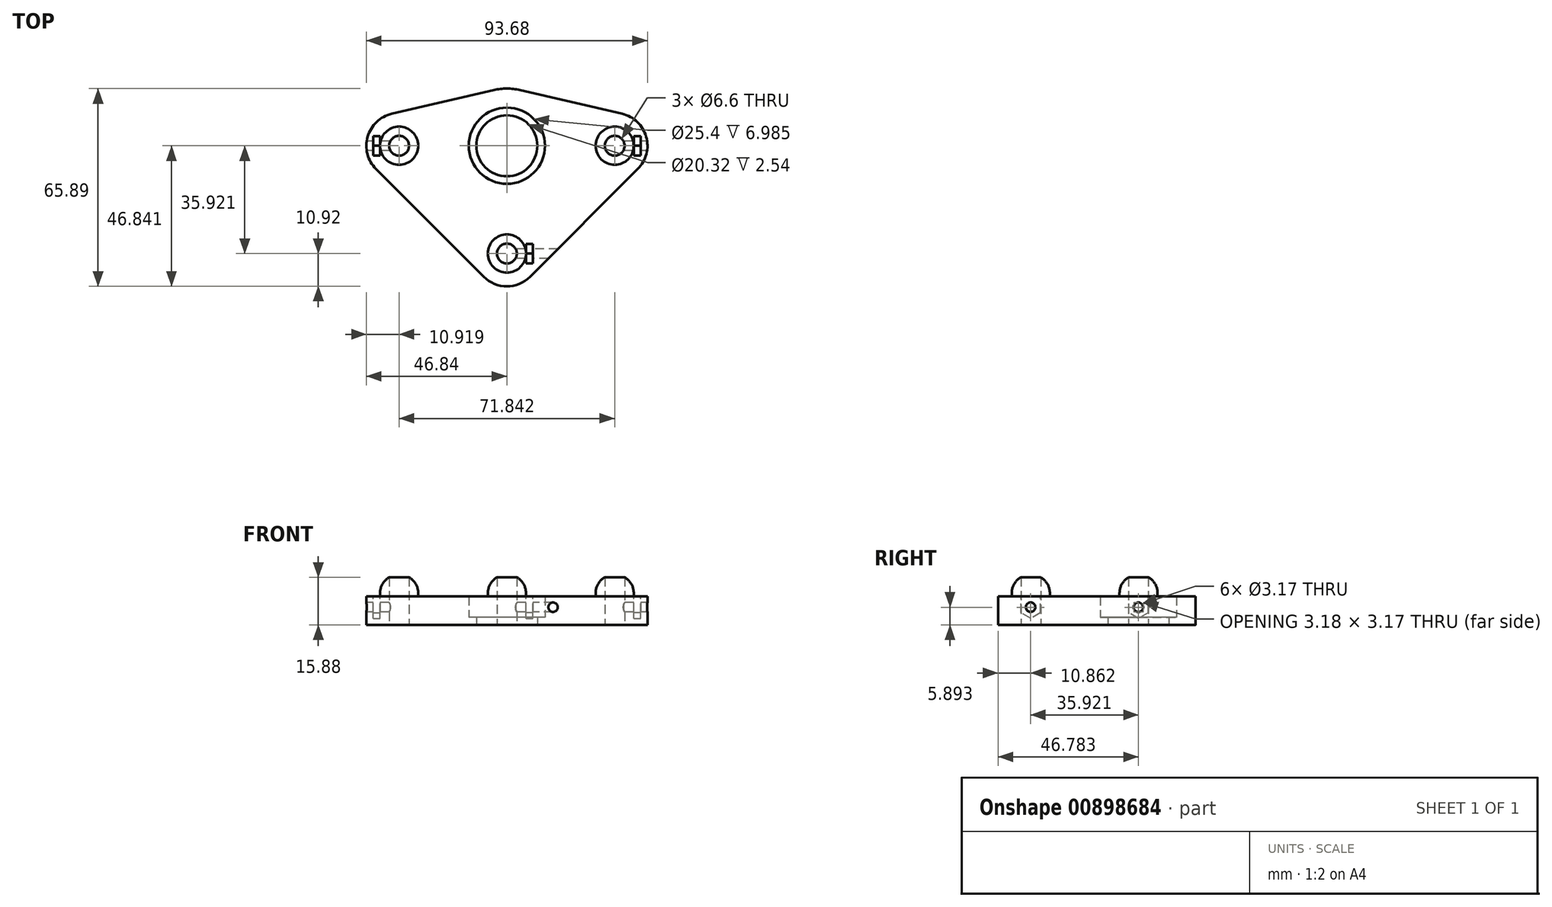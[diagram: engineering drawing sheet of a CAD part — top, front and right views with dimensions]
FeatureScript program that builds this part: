
annotation { "Feature Type Name" : "Feature", "Feature Type Description" : "" }
export const myFeature = defineFeature(function(context is Context, id is Id, definition is map)
    precondition{}
    {
        {
            var Q0;
            Q0=qCreatedBy(makeId("Top.planeOp"),FACE);
            var sketch = newSketch(context, id + "F0", { "sketchPlane" : qUnion([Q0])});
            skCircle(sketch, "E0", {"center": v(0, 35.92) * mm, "radius": 12.7 * mm});
            skArc(sketch, "E1.0", {"start": v(4.31, 54.48) * mm, "mid": v(0, 54.97) * mm, "end": v(-4.31, 54.48) * mm});
            skLineSegment(sketch, "E2", {"start": v(-38.4, 46.56) * mm, "end": v(-4.31, 54.48) * mm});
            skLineSegment(sketch, "E3", {"start": v(4.31, 54.48) * mm, "end": v(38.4, 46.56) * mm});
            skCircle(sketch, "E4.0", {"center": v(0, 35.92) * mm, "radius": 10.16 * mm});
            skLineSegment(sketch, "E5", {"start": v(0, 35.92) * mm, "end": v(0, 48.62) * mm, "construction": true});
            skLineSegment(sketch, "E6", {"start": v(-35.92, 35.92) * mm, "end": v(35.92, 35.92) * mm, "construction": true});
            skCircle(sketch, "E7", {"center": v(0, 0) * mm, "radius": 3.3 * mm});
            skCircle(sketch, "E8", {"center": v(35.92, 35.92) * mm, "radius": 3.3 * mm});
            skCircle(sketch, "E9", {"center": v(-35.92, 35.92) * mm, "radius": 3.3 * mm});
            skArc(sketch, "E10.0", {"start": v(-38.4, 46.56) * mm, "mid": v(-46.42, 38.92) * mm, "end": v(-43.64, 28.2) * mm});
            skArc(sketch, "E11.0", {"start": v(-7.72, -7.72) * mm, "mid": v(0, -10.92) * mm, "end": v(7.72, -7.72) * mm});
            skArc(sketch, "E12.0", {"start": v(43.64, 28.2) * mm, "mid": v(46.42, 38.92) * mm, "end": v(38.4, 46.56) * mm});
            skLineSegment(sketch, "E13", {"start": v(-43.64, 28.2) * mm, "end": v(-7.72, -7.72) * mm});
            skLineSegment(sketch, "E14", {"start": v(7.72, -7.72) * mm, "end": v(43.64, 28.2) * mm});
            skSolve(sketch);
        }
        {
            var Q0;
            Q0=makeQuery(id+"F0.imprint","IMPRINT",FACE,{"disambiguationData":[TD([[makeQuery(id+"F0.imprint","IMPRINT",EDGE,{"derivedFrom":sQuery(id+"F0.wireOp",EDGE,"E0")}),-1.0]])]});
            extrude(context, id + "F1", {"entities" : qUnion([Q0]), "depth" : 9.52 * mm, "offsetDistance" : 25.4 * mm});
        }
        {
            var Q0;
            Q0=makeQuery(id+"F0.imprint","IMPRINT",FACE,{"disambiguationData":[TD([[makeQuery(id+"F0.imprint","IMPRINT",EDGE,{"derivedFrom":sQuery(id+"F0.wireOp",EDGE,"E0")}),1.0]])]});
            var Q1;
            Q1=makeQuery(id+"F1.opExtrude","CAP_FACE",FACE,{"disambiguationData":[OSD([sQuery(id+"F0.wireOp",EDGE,"EjYE8rPL-0voM-13ep-dpKR-Yhmu4oC0fMjX"),sQuery(id+"F0.wireOp",EDGE,"BDsdlpYl-4XZS-kb72-SQzJ-jy24um5DGsSm"),sQuery(id+"F0.wireOp",EDGE,"zDj9rnkT-zBYQ-YRrf-FuGE-prHvdQQL9E0l"),sQuery(id+"F0.wireOp",EDGE,"E0"),sQuery(id+"F0.wireOp",EDGE,"be656b23-60e4-4951-9072-4bb9fd2c1fe0.0"),sQuery(id+"F0.wireOp",EDGE,"E1.0"),sQuery(id+"F0.wireOp",EDGE,"4a9f2f50-e787-4006-96f4-ab8e54a99077.0"),sQuery(id+"F0.wireOp",EDGE,"02fbeba7-076e-4ed0-9f02-67362b93dccf.0"),sQuery(id+"F0.wireOp",EDGE,"E2"),sQuery(id+"F0.wireOp",EDGE,"E3"),sQuery(id+"F0.wireOp",EDGE,"O9yRHGw0-B6N5-WUBC-CqYZ-9fVMz9zkHXct"),sQuery(id+"F0.wireOp",EDGE,"bXI39tXD-kIKO-QA8d-uo1d-AjNWw4kzWSzn"),sQuery(id+"F0.wireOp",EDGE,"yvXXFvSa-JQHm-aZvy-wO3q-0ffgoC5Wr51Q"),sQuery(id+"F0.wireOp",EDGE,"keBa6mA6-Ns36-as4S-D7yK-ubB9MYcM4YDE"),sQuery(id+"F0.wireOp",EDGE,"8eHimBAp-EooJ-JMgW-8GNK-FZK91k5yhUmU"),sQuery(id+"F0.wireOp",EDGE,"36RZBXD3-6qK0-qw5N-QxHJ-8RBiURi620yN"),sQuery(id+"F0.wireOp",EDGE,"1b80de2d-6fcf-4166-8bd7-bc7520118ab3.trimOffspring"),sQuery(id+"F0.wireOp",EDGE,"c2b8b45b-57a7-46a8-b7ff-993cbbd2993e.trimOffspring"),sQuery(id+"F0.wireOp",EDGE,"9e57da74-859c-4f91-937b-fdcaf8afdda5.filletArc"),sQuery(id+"F0.wireOp",EDGE,"30e6a12d-ff62-4460-809b-2951cf116d4f.filletArc"),sQuery(id+"F0.wireOp",EDGE,"3d167f00-72a4-4ff5-8a6d-0d591a0e7773.filletArc"),sQuery(id+"F0.wireOp",EDGE,"oY1VHBi5-08zZ-AYfj-pQcV-54PoHM0Vimur"),sQuery(id+"F0.wireOp",EDGE,"o9Ub0ZbI-FWSb-Ar0A-mzkB-0TMMgAmCBTNA"),sQuery(id+"F0.wireOp",EDGE,"02ed80ea-b338-46f1-988c-5186e078d909.trimOffspring"),sQuery(id+"F0.wireOp",EDGE,"5048e359-dd0b-4d89-8e95-103b38747b91.filletArc"),sQuery(id+"F0.wireOp",EDGE,"F9NU9Cbi-ggXa-7yM7-VtZo-IDbmedrVVywU"),sQuery(id+"F0.wireOp",EDGE,"RxFEJMYw-qQQS-0Qhc-ig3X-IfwXJgG6lVj4"),sQuery(id+"F0.wireOp",EDGE,"25558c64-657d-4b99-b26e-c29775e7ec7f.filletArc"),sQuery(id+"F0.wireOp",EDGE,"0ec6c237-3fc5-43e5-bd65-df81ba4ec1d8.filletArc"),sQuery(id+"F0.wireOp",EDGE,"df5fecd0-7309-4179-a44a-8c306f083116.filletArc"),sQuery(id+"F0.wireOp",EDGE,"e0a676b0-1f90-490a-bc8b-b1ab685ed8d2.filletArc")])],"isStart":false});
            extrude(context, id + "F2", {"entities" : qUnion([Q0]), "operationType" : NewBodyOperationType.ADD, "depth" : 2.54 * mm, "endBoundEntityFace" : qUnion([Q1]), "offsetDistance" : 6.35 * mm});
        }
        {
            var Q0;
            Q0=makeQuery(id+"F1.opExtrude","CAP_FACE",FACE,{"disambiguationData":[OSD([sQuery(id+"F0.wireOp",EDGE,"EjYE8rPL-0voM-13ep-dpKR-Yhmu4oC0fMjX"),sQuery(id+"F0.wireOp",EDGE,"BDsdlpYl-4XZS-kb72-SQzJ-jy24um5DGsSm"),sQuery(id+"F0.wireOp",EDGE,"zDj9rnkT-zBYQ-YRrf-FuGE-prHvdQQL9E0l"),sQuery(id+"F0.wireOp",EDGE,"E0"),sQuery(id+"F0.wireOp",EDGE,"be656b23-60e4-4951-9072-4bb9fd2c1fe0.0"),sQuery(id+"F0.wireOp",EDGE,"E1.0"),sQuery(id+"F0.wireOp",EDGE,"4a9f2f50-e787-4006-96f4-ab8e54a99077.0"),sQuery(id+"F0.wireOp",EDGE,"02fbeba7-076e-4ed0-9f02-67362b93dccf.0"),sQuery(id+"F0.wireOp",EDGE,"E2"),sQuery(id+"F0.wireOp",EDGE,"E3"),sQuery(id+"F0.wireOp",EDGE,"O9yRHGw0-B6N5-WUBC-CqYZ-9fVMz9zkHXct"),sQuery(id+"F0.wireOp",EDGE,"bXI39tXD-kIKO-QA8d-uo1d-AjNWw4kzWSzn"),sQuery(id+"F0.wireOp",EDGE,"yvXXFvSa-JQHm-aZvy-wO3q-0ffgoC5Wr51Q"),sQuery(id+"F0.wireOp",EDGE,"keBa6mA6-Ns36-as4S-D7yK-ubB9MYcM4YDE"),sQuery(id+"F0.wireOp",EDGE,"8eHimBAp-EooJ-JMgW-8GNK-FZK91k5yhUmU"),sQuery(id+"F0.wireOp",EDGE,"36RZBXD3-6qK0-qw5N-QxHJ-8RBiURi620yN"),sQuery(id+"F0.wireOp",EDGE,"1b80de2d-6fcf-4166-8bd7-bc7520118ab3.trimOffspring"),sQuery(id+"F0.wireOp",EDGE,"c2b8b45b-57a7-46a8-b7ff-993cbbd2993e.trimOffspring"),sQuery(id+"F0.wireOp",EDGE,"9e57da74-859c-4f91-937b-fdcaf8afdda5.filletArc"),sQuery(id+"F0.wireOp",EDGE,"30e6a12d-ff62-4460-809b-2951cf116d4f.filletArc"),sQuery(id+"F0.wireOp",EDGE,"3d167f00-72a4-4ff5-8a6d-0d591a0e7773.filletArc"),sQuery(id+"F0.wireOp",EDGE,"oY1VHBi5-08zZ-AYfj-pQcV-54PoHM0Vimur"),sQuery(id+"F0.wireOp",EDGE,"o9Ub0ZbI-FWSb-Ar0A-mzkB-0TMMgAmCBTNA"),sQuery(id+"F0.wireOp",EDGE,"02ed80ea-b338-46f1-988c-5186e078d909.trimOffspring"),sQuery(id+"F0.wireOp",EDGE,"3LgmcLzA-5pnU-fFz7-q1u9-bpeBtAsCO3An"),sQuery(id+"F0.wireOp",EDGE,"4eo9xTR6-c1Fu-en91-zOid-S4E7wj55DmDX"),sQuery(id+"F0.wireOp",EDGE,"5048e359-dd0b-4d89-8e95-103b38747b91.filletArc"),sQuery(id+"F0.wireOp",EDGE,"0de4be46-af92-408f-a28e-b5eb566cc358.filletArc"),sQuery(id+"F0.wireOp",EDGE,"cd97e584-8722-4711-bad1-4d169eb79cda.filletArc"),sQuery(id+"F0.wireOp",EDGE,"a80f9f6f-3806-41d0-9fd0-596e0330244b.filletArc"),sQuery(id+"F0.wireOp",EDGE,"743a1c7c-530f-41f0-bede-06812bb20fe3.filletArc")])],"isStart":false});
            var sketch = newSketch(context, id + "F3", { "sketchPlane" : qUnion([Q0])});
            skCircle(sketch, "E15", {"center": v(-35.92, 35.92) * mm, "radius": 6.35 * mm});
            skCircle(sketch, "E16", {"center": v(35.92, 35.92) * mm, "radius": 6.35 * mm});
            skCircle(sketch, "E17", {"center": v(0, 0) * mm, "radius": 6.35 * mm});
            skSolve(sketch);
        }
        {
            var Q0;
            Q0=makeQuery(id+"F1.opExtrude","CAP_FACE",FACE,{"disambiguationData":[OSD([sQuery(id+"F0.wireOp",EDGE,"EjYE8rPL-0voM-13ep-dpKR-Yhmu4oC0fMjX"),sQuery(id+"F0.wireOp",EDGE,"BDsdlpYl-4XZS-kb72-SQzJ-jy24um5DGsSm"),sQuery(id+"F0.wireOp",EDGE,"zDj9rnkT-zBYQ-YRrf-FuGE-prHvdQQL9E0l"),sQuery(id+"F0.wireOp",EDGE,"E0"),sQuery(id+"F0.wireOp",EDGE,"be656b23-60e4-4951-9072-4bb9fd2c1fe0.0"),sQuery(id+"F0.wireOp",EDGE,"E1.0"),sQuery(id+"F0.wireOp",EDGE,"4a9f2f50-e787-4006-96f4-ab8e54a99077.0"),sQuery(id+"F0.wireOp",EDGE,"02fbeba7-076e-4ed0-9f02-67362b93dccf.0"),sQuery(id+"F0.wireOp",EDGE,"E2"),sQuery(id+"F0.wireOp",EDGE,"E3"),sQuery(id+"F0.wireOp",EDGE,"O9yRHGw0-B6N5-WUBC-CqYZ-9fVMz9zkHXct"),sQuery(id+"F0.wireOp",EDGE,"bXI39tXD-kIKO-QA8d-uo1d-AjNWw4kzWSzn"),sQuery(id+"F0.wireOp",EDGE,"yvXXFvSa-JQHm-aZvy-wO3q-0ffgoC5Wr51Q"),sQuery(id+"F0.wireOp",EDGE,"keBa6mA6-Ns36-as4S-D7yK-ubB9MYcM4YDE"),sQuery(id+"F0.wireOp",EDGE,"8eHimBAp-EooJ-JMgW-8GNK-FZK91k5yhUmU"),sQuery(id+"F0.wireOp",EDGE,"36RZBXD3-6qK0-qw5N-QxHJ-8RBiURi620yN"),sQuery(id+"F0.wireOp",EDGE,"1b80de2d-6fcf-4166-8bd7-bc7520118ab3.trimOffspring"),sQuery(id+"F0.wireOp",EDGE,"c2b8b45b-57a7-46a8-b7ff-993cbbd2993e.trimOffspring"),sQuery(id+"F0.wireOp",EDGE,"9e57da74-859c-4f91-937b-fdcaf8afdda5.filletArc"),sQuery(id+"F0.wireOp",EDGE,"2f08ad09-a47d-42bd-8f0e-b7f58f6490e4.filletArc"),sQuery(id+"F0.wireOp",EDGE,"30e6a12d-ff62-4460-809b-2951cf116d4f.filletArc"),sQuery(id+"F0.wireOp",EDGE,"3d167f00-72a4-4ff5-8a6d-0d591a0e7773.filletArc"),sQuery(id+"F0.wireOp",EDGE,"oY1VHBi5-08zZ-AYfj-pQcV-54PoHM0Vimur"),sQuery(id+"F0.wireOp",EDGE,"o9Ub0ZbI-FWSb-Ar0A-mzkB-0TMMgAmCBTNA"),sQuery(id+"F0.wireOp",EDGE,"02ed80ea-b338-46f1-988c-5186e078d909.trimOffspring"),sQuery(id+"F0.wireOp",EDGE,"bfc3d6b4-ed7b-404a-8939-94d15189dd00.filletArc"),sQuery(id+"F0.wireOp",EDGE,"d06de643-c4a7-4e1d-b592-4d839de3a7a0.filletArc")])],"isStart":false});
            var sketch = newSketch(context, id + "F4", { "sketchPlane" : qUnion([Q0])});
            skPoint(sketch, "E18.center", {"position": v(0, 35.92) * mm});
            skCircle(sketch, "E19", {"center": v(-35.92, 35.92) * mm, "radius": 6.35 * mm});
            skCircle(sketch, "E20", {"center": v(35.92, 35.92) * mm, "radius": 6.35 * mm});
            skCircle(sketch, "E21", {"center": v(0, 0) * mm, "radius": 6.35 * mm});
            skLineSegment(sketch, "E22", {"start": v(-42.27, 39.15) * mm, "end": v(-42.27, 32.7) * mm});
            skLineSegment(sketch, "E23", {"start": v(-42.27, 32.7) * mm, "end": v(-44.6, 32.7) * mm});
            skLineSegment(sketch, "E24", {"start": v(-44.6, 32.7) * mm, "end": v(-44.6, 39.15) * mm});
            skLineSegment(sketch, "E25", {"start": v(-44.6, 39.15) * mm, "end": v(-42.27, 39.15) * mm});
            skLineSegment(sketch, "E26", {"start": v(-35.92, 35.92) * mm, "end": v(-42.27, 35.92) * mm, "construction": true});
            skLineSegment(sketch, "E27", {"start": v(42.27, 32.7) * mm, "end": v(42.27, 39.15) * mm});
            skLineSegment(sketch, "E28", {"start": v(42.27, 39.15) * mm, "end": v(44.6, 39.15) * mm});
            skLineSegment(sketch, "E29", {"start": v(44.6, 39.15) * mm, "end": v(44.6, 32.7) * mm});
            skLineSegment(sketch, "E30", {"start": v(44.6, 32.7) * mm, "end": v(42.27, 32.7) * mm});
            skLineSegment(sketch, "E31", {"start": v(35.92, 35.92) * mm, "end": v(42.27, 35.92) * mm, "construction": true});
            skLineSegment(sketch, "E32", {"start": v(8.69, 3.23) * mm, "end": v(8.69, -3.23) * mm});
            skLineSegment(sketch, "E33", {"start": v(8.69, -3.23) * mm, "end": v(6.35, -3.23) * mm});
            skLineSegment(sketch, "E34", {"start": v(6.35, -3.23) * mm, "end": v(6.35, 3.23) * mm});
            skLineSegment(sketch, "E35", {"start": v(6.35, 3.23) * mm, "end": v(8.69, 3.23) * mm});
            skLineSegment(sketch, "E36", {"start": v(8.69, 0) * mm, "end": v(0, 0) * mm, "construction": true});
            skSolve(sketch);
        }
        {
            var Q0;
            Q0=makeQuery(id+"F4.imprint","IMPRINT",FACE,{"disambiguationData":[TD([[makeQuery(id+"F4.imprint","IMPRINT",EDGE,{"derivedFrom":sQuery(id+"F4.wireOp",EDGE,"E18.2.0")}),-1.0]])]});
            var Q1;
            {var subQ3=sQuery(id+"F4.wireOp",EDGE,"d1FFw4VD-CotE-ErUC-aBlM-ySrozfUtPZIG");Q1=makeQuery(id+"F4.imprint","IMPRINT",FACE,{"disambiguationData":[TD([[makeQuery(id+"F4.imprint","IMPRINT",EDGE,{"derivedFrom":subQ3}),-1.0]])]});}
            var Q2;
            Q2=makeQuery(id+"F4.imprint","IMPRINT",FACE,{"disambiguationData":[TD([[makeQuery(id+"F4.imprint","IMPRINT",EDGE,{"derivedFrom":sQuery(id+"F4.wireOp",EDGE,"E18.1.0")}),-1.0]])]});
            var Q3;
            {var subQ0=sQuery(id+"F4.wireOp",EDGE,"E23");Q3=makeQuery(id+"F4.imprint","IMPRINT",FACE,{"disambiguationData":[TD([[makeQuery(id+"F4.imprint","IMPRINT",EDGE,{"derivedFrom":subQ0}),-1.0]])]});}
            var Q4;
            {var subQ0=sQuery(id+"F4.wireOp",EDGE,"E28");Q4=makeQuery(id+"F4.imprint","IMPRINT",FACE,{"disambiguationData":[TD([[makeQuery(id+"F4.imprint","IMPRINT",EDGE,{"derivedFrom":subQ0}),-1.0]])]});}
            var Q5;
            Q5=makeQuery(id+"F4.imprint","IMPRINT",FACE,{"disambiguationData":[TD([[makeQuery(id+"F4.imprint","IMPRINT",EDGE,{"derivedFrom":sQuery(id+"F4.wireOp",EDGE,"E32")}),-1.0]])]});
            extrude(context, id + "F5", {"entities" : qUnion([Q0, Q1, Q2, Q3, Q4, Q5]), "operationType" : NewBodyOperationType.REMOVE, "oppositeDirection" : true, "depth" : 8.64 * mm, "offsetDistance" : 25.4 * mm});
        }
        {
            var Q0;
            Q0=makeQuery(id+"F5.boolean.opBoolean","COPY",EDGE,{"derivedFrom":makeQuery(id+"F5.opExtrude","CAP_EDGE",EDGE,{"disambiguationData":[OSD([sQuery(id+"F4.wireOp",EDGE,"E18.1.1")])],"isStart":false})});
            var Q1;
            Q1=makeQuery(id+"F5.boolean.opBoolean","COPY",EDGE,{"derivedFrom":makeQuery(id+"F5.opExtrude","CAP_EDGE",EDGE,{"disambiguationData":[OSD([sQuery(id+"F4.wireOp",EDGE,"E18.1.3")])],"isStart":false})});
            var Q2;
            Q2=makeQuery(id+"F5.boolean.opBoolean","COPY",EDGE,{"derivedFrom":makeQuery(id+"F5.opExtrude","CAP_EDGE",EDGE,{"disambiguationData":[OSD([sQuery(id+"F4.wireOp",EDGE,"d1FFw4VD-CotE-ErUC-aBlM-ySrozfUtPZIG")])],"isStart":false})});
            var Q3;
            Q3=makeQuery(id+"F5.boolean.opBoolean","COPY",EDGE,{"derivedFrom":makeQuery(id+"F5.opExtrude","CAP_EDGE",EDGE,{"disambiguationData":[OSD([sQuery(id+"F4.wireOp",EDGE,"UtWCcdUI-wfrM-d3JI-pGr6-eE53RfRw4Zsa")])],"isStart":false})});
            var Q4;
            Q4=makeQuery(id+"F5.boolean.opBoolean","COPY",EDGE,{"derivedFrom":makeQuery(id+"F5.opExtrude","CAP_EDGE",EDGE,{"disambiguationData":[OSD([sQuery(id+"F4.wireOp",EDGE,"E18.2.3")])],"isStart":false})});
            var Q5;
            Q5=makeQuery(id+"F5.boolean.opBoolean","COPY",EDGE,{"derivedFrom":makeQuery(id+"F5.opExtrude","CAP_EDGE",EDGE,{"disambiguationData":[OSD([sQuery(id+"F4.wireOp",EDGE,"E18.2.1")])],"isStart":false})});
            var Q6;
            Q6=makeQuery(id+"F5.boolean.opBoolean","COPY",EDGE,{"derivedFrom":makeQuery(id+"F5.opExtrude","CAP_EDGE",EDGE,{"disambiguationData":[OSD([sQuery(id+"F4.wireOp",EDGE,"E25")])],"isStart":false})});
            var Q7;
            Q7=makeQuery(id+"F5.boolean.opBoolean","COPY",EDGE,{"derivedFrom":makeQuery(id+"F5.opExtrude","CAP_EDGE",EDGE,{"disambiguationData":[OSD([sQuery(id+"F4.wireOp",EDGE,"E23")])],"isStart":false})});
            var Q8;
            Q8=makeQuery(id+"F5.boolean.opBoolean","COPY",EDGE,{"derivedFrom":makeQuery(id+"F5.opExtrude","CAP_EDGE",EDGE,{"disambiguationData":[OSD([sQuery(id+"F4.wireOp",EDGE,"E35")])],"isStart":false})});
            var Q9;
            Q9=makeQuery(id+"F5.boolean.opBoolean","COPY",EDGE,{"derivedFrom":makeQuery(id+"F5.opExtrude","CAP_EDGE",EDGE,{"disambiguationData":[OSD([sQuery(id+"F4.wireOp",EDGE,"E33")])],"isStart":false})});
            var Q10;
            Q10=makeQuery(id+"F5.boolean.opBoolean","COPY",EDGE,{"derivedFrom":makeQuery(id+"F5.opExtrude","CAP_EDGE",EDGE,{"disambiguationData":[OSD([sQuery(id+"F4.wireOp",EDGE,"E28")])],"isStart":false})});
            var Q11;
            Q11=makeQuery(id+"F5.boolean.opBoolean","COPY",EDGE,{"derivedFrom":makeQuery(id+"F5.opExtrude","CAP_EDGE",EDGE,{"disambiguationData":[OSD([sQuery(id+"F4.wireOp",EDGE,"E30")])],"isStart":false})});
            chamfer(context, id + "F6", {"entities" : qUnion([Q0, Q1, Q2, Q3, Q4, Q5, Q6, Q7, Q8, Q9, Q10, Q11]), "chamferType" : ChamferType.OFFSET_ANGLE, "width" : 3.17 * mm, "oppositeDirection" : false, "angle" : 60 * degree, "tangentPropagation" : true});
        }
        {
            var Q0;
            Q0=makeQuery(id+"F3.imprint","IMPRINT",FACE,{"disambiguationData":[TD([[makeQuery(id+"F3.imprint","IMPRINT",EDGE,{"derivedFrom":sQuery(id+"F3.wireOp",EDGE,"E15")}),1.0]])]});
            var Q1;
            Q1=makeQuery(id+"F3.imprint","IMPRINT",FACE,{"disambiguationData":[TD([[makeQuery(id+"F3.imprint","IMPRINT",EDGE,{"derivedFrom":sQuery(id+"F3.wireOp",EDGE,"E17")}),1.0]])]});
            var Q2;
            Q2=makeQuery(id+"F3.imprint","IMPRINT",FACE,{"disambiguationData":[TD([[makeQuery(id+"F3.imprint","IMPRINT",EDGE,{"derivedFrom":sQuery(id+"F3.wireOp",EDGE,"E16")}),1.0]])]});
            extrude(context, id + "F7", {"entities" : qUnion([Q0, Q1, Q2]), "operationType" : NewBodyOperationType.ADD, "depth" : 6.35 * mm, "offsetDistance" : 25.4 * mm});
        }
        {
            var Q0;
            Q0=makeQuery(id+"F7.opExtrude","CAP_EDGE",EDGE,{"disambiguationData":[OSD([sQuery(id+"F3.wireOp",EDGE,"E15")])],"isStart":false});
            var Q1;
            Q1=makeQuery(id+"F7.opExtrude","CAP_EDGE",EDGE,{"disambiguationData":[OSD([sQuery(id+"F3.wireOp",EDGE,"E16")])],"isStart":false});
            var Q2;
            Q2=makeQuery(id+"F7.opExtrude","CAP_EDGE",EDGE,{"disambiguationData":[OSD([sQuery(id+"F3.wireOp",EDGE,"E17")])],"isStart":false});
            fillet(context, id + "F8", {"entities" : qUnion([Q0, Q1, Q2]), "radius" : 6.1 * mm, "tangentPropagation" : true, "allowEdgeOverflow" : false});
        }
        {
            var Q0;
            Q0=makeQuery(id+"F5.boolean.opBoolean","COPY",FACE,{"derivedFrom":makeQuery(id+"F5.opExtrude","SWEPT_FACE",FACE,{"disambiguationData":[OSD([sQuery(id+"F4.wireOp",EDGE,"E24")])]})});
            var sketch = newSketch(context, id + "F9", { "sketchPlane" : qUnion([Q0])});
            skLineSegment(sketch, "E37", {"start": v(39.03, 4.06) * mm, "end": v(35.86, 2.24) * mm});
            skLineSegment(sketch, "E38", {"start": v(35.86, 2.24) * mm, "end": v(32.7, 4.06) * mm});
            skLineSegment(sketch, "E39", {"start": v(32.7, 4.06) * mm, "end": v(32.7, 7.72) * mm});
            skLineSegment(sketch, "E40", {"start": v(39.03, 7.72) * mm, "end": v(39.03, 4.06) * mm});
            skLineSegment(sketch, "E41", {"start": v(39.03, 7.72) * mm, "end": v(35.86, 9.55) * mm});
            skLineSegment(sketch, "E42", {"start": v(35.86, 9.55) * mm, "end": v(32.7, 7.72) * mm});
            skLineSegment(sketch, "E43", {"start": v(35.86, 2.24) * mm, "end": v(35.86, 5.9) * mm, "construction": true});
            skLineSegment(sketch, "E44", {"start": v(35.86, 5.9) * mm, "end": v(32.7, 4.06) * mm, "construction": true});
            skLineSegment(sketch, "E45", {"start": v(35.86, 5.9) * mm, "end": v(39.03, 7.72) * mm, "construction": true});
            skLineSegment(sketch, "E46", {"start": v(35.86, 5.9) * mm, "end": v(35.86, 9.55) * mm, "construction": true});
            skCircle(sketch, "E47", {"center": v(35.86, 5.9) * mm, "radius": 1.59 * mm});
            skSolve(sketch);
        }
        {
            var Q0;
            Q0=makeQuery(id+"F5.boolean.opBoolean","COPY",FACE,{"derivedFrom":makeQuery(id+"F5.opExtrude","SWEPT_FACE",FACE,{"disambiguationData":[OSD([sQuery(id+"F4.wireOp",EDGE,"E32")])]})});
            var sketch = newSketch(context, id + "F10", { "sketchPlane" : qUnion([Q0])});
            skLineSegment(sketch, "E48", {"start": v(3.23, 4.06) * mm, "end": v(0.06, 2.24) * mm});
            skLineSegment(sketch, "E49", {"start": v(0.06, 2.24) * mm, "end": v(-3.1, 4.06) * mm});
            skLineSegment(sketch, "E50", {"start": v(-3.1, 4.06) * mm, "end": v(-3.1, 7.72) * mm});
            skLineSegment(sketch, "E51", {"start": v(3.23, 7.72) * mm, "end": v(3.23, 4.06) * mm});
            skLineSegment(sketch, "E52", {"start": v(3.23, 7.72) * mm, "end": v(0.06, 9.55) * mm});
            skLineSegment(sketch, "E53", {"start": v(0.06, 9.55) * mm, "end": v(-3.1, 7.72) * mm});
            skLineSegment(sketch, "E54", {"start": v(0.06, 2.24) * mm, "end": v(0.06, 5.9) * mm, "construction": true});
            skLineSegment(sketch, "E55", {"start": v(0.06, 5.9) * mm, "end": v(-3.1, 4.06) * mm, "construction": true});
            skLineSegment(sketch, "E56", {"start": v(0.06, 5.9) * mm, "end": v(3.23, 7.72) * mm, "construction": true});
            skLineSegment(sketch, "E57", {"start": v(0.06, 5.9) * mm, "end": v(0.06, 9.55) * mm, "construction": true});
            skCircle(sketch, "E58", {"center": v(0.06, 5.9) * mm, "radius": 1.59 * mm});
            skSolve(sketch);
        }
        {
            var Q0;
            Q0=makeQuery(id+"F5.boolean.opBoolean","COPY",FACE,{"derivedFrom":makeQuery(id+"F5.opExtrude","SWEPT_FACE",FACE,{"disambiguationData":[OSD([sQuery(id+"F4.wireOp",EDGE,"E29")])]})});
            var sketch = newSketch(context, id + "F11", { "sketchPlane" : qUnion([Q0])});
            skLineSegment(sketch, "E59", {"start": v(-32.7, 4.06) * mm, "end": v(-35.86, 2.24) * mm});
            skLineSegment(sketch, "E60", {"start": v(-35.86, 2.24) * mm, "end": v(-39.03, 4.06) * mm});
            skLineSegment(sketch, "E61", {"start": v(-39.03, 4.06) * mm, "end": v(-39.03, 7.72) * mm});
            skLineSegment(sketch, "E62", {"start": v(-32.7, 7.72) * mm, "end": v(-32.7, 4.06) * mm});
            skLineSegment(sketch, "E63", {"start": v(-32.7, 7.72) * mm, "end": v(-35.86, 9.55) * mm});
            skLineSegment(sketch, "E64", {"start": v(-35.86, 9.55) * mm, "end": v(-39.03, 7.72) * mm});
            skLineSegment(sketch, "E65", {"start": v(-35.86, 2.24) * mm, "end": v(-35.86, 5.9) * mm, "construction": true});
            skLineSegment(sketch, "E66", {"start": v(-35.86, 5.9) * mm, "end": v(-39.03, 4.06) * mm, "construction": true});
            skLineSegment(sketch, "E67", {"start": v(-35.86, 5.9) * mm, "end": v(-32.7, 7.72) * mm, "construction": true});
            skLineSegment(sketch, "E68", {"start": v(-35.86, 5.9) * mm, "end": v(-35.86, 9.55) * mm, "construction": true});
            skCircle(sketch, "E69", {"center": v(-35.86, 5.9) * mm, "radius": 1.59 * mm});
            skSolve(sketch);
        }
        {
            var Q0;
            Q0=makeQuery(id+"F11.imprint","IMPRINT",FACE,{"disambiguationData":[TD([[makeQuery(id+"F11.imprint","IMPRINT",EDGE,{"derivedFrom":sQuery(id+"F11.wireOp",EDGE,"E69")}),1.0]])]});
            var Q1;
            Q1=sQuery(id+"F11.wireOp",EDGE,"E69");
            extrude(context, id + "F12", {"entities" : qUnion([Q0]), "operationType" : NewBodyOperationType.REMOVE, "surfaceEntities" : qUnion([Q1]), "oppositeDirection" : true, "depth" : 12.7 * mm, "offsetDistance" : 25.4 * mm, "symmetric" : true});
        }
        {
            var Q0;
            Q0=makeQuery(id+"F9.imprint","IMPRINT",FACE,{"disambiguationData":[TD([[makeQuery(id+"F9.imprint","IMPRINT",EDGE,{"derivedFrom":sQuery(id+"F9.wireOp",EDGE,"E47")}),1.0]])]});
            extrude(context, id + "F13", {"entities" : qUnion([Q0]), "operationType" : NewBodyOperationType.REMOVE, "depth" : 12.7 * mm, "offsetDistance" : 25.4 * mm, "symmetric" : true});
        }
        {
            var Q0;
            Q0=makeQuery(id+"F10.imprint","IMPRINT",FACE,{"disambiguationData":[TD([[makeQuery(id+"F10.imprint","IMPRINT",EDGE,{"derivedFrom":sQuery(id+"F10.wireOp",EDGE,"E58")}),1.0]])]});
            extrude(context, id + "F14", {"entities" : qUnion([Q0]), "operationType" : NewBodyOperationType.REMOVE, "oppositeDirection" : true, "depth" : 16.76 * mm, "offsetDistance" : 25.4 * mm, "symmetric" : true});
        }
    });
